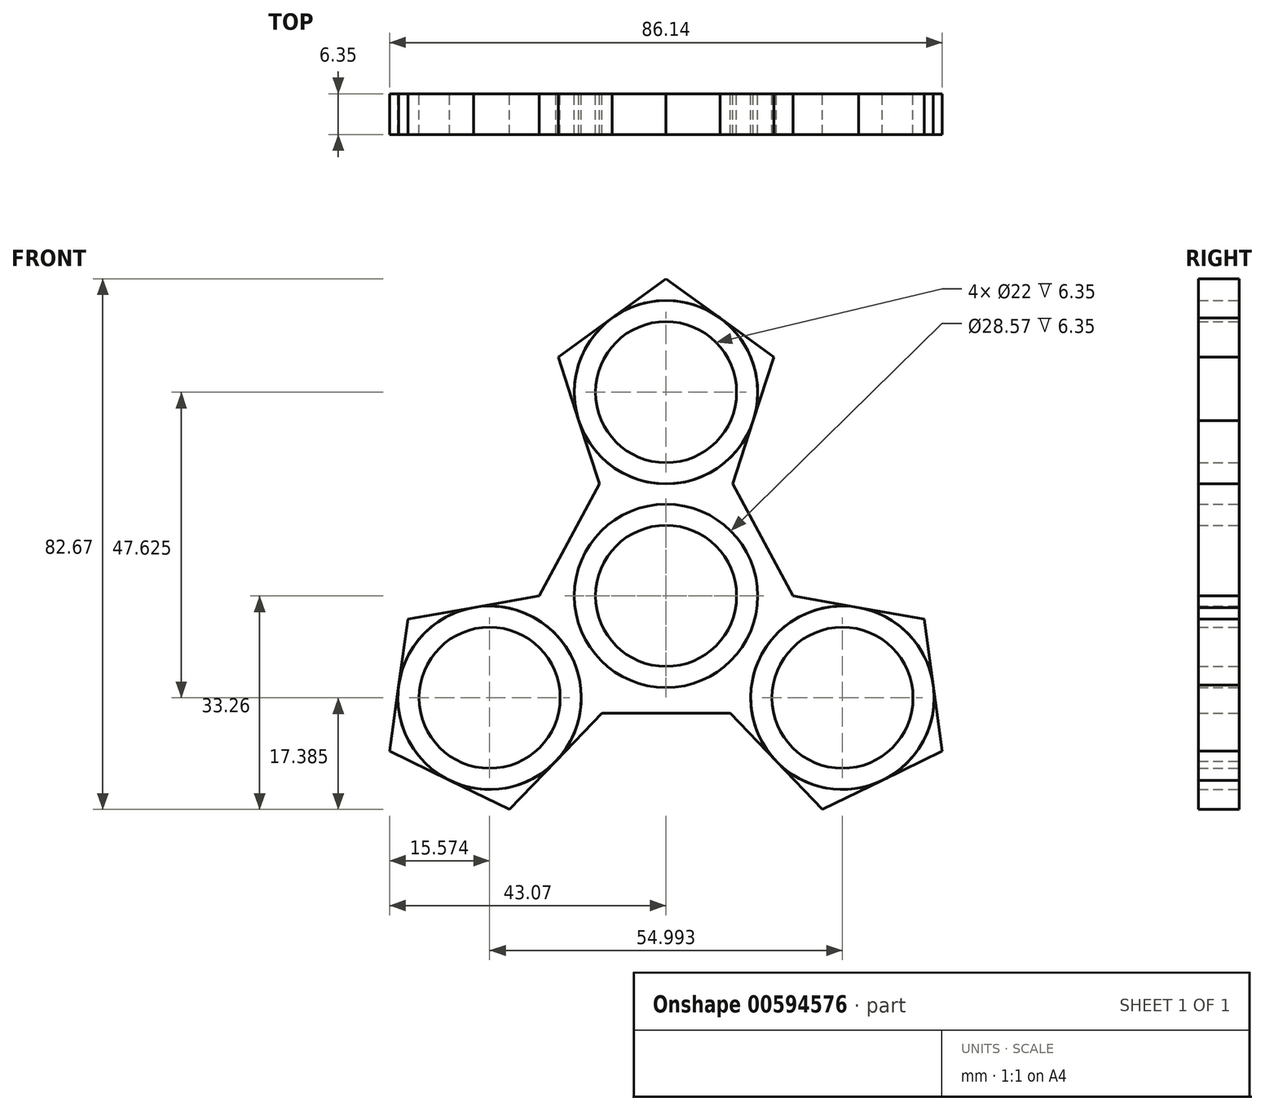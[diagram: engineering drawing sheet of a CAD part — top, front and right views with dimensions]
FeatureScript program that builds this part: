
annotation { "Feature Type Name" : "Feature", "Feature Type Description" : "" }
export const myFeature = defineFeature(function(context is Context, id is Id, definition is map)
    precondition{}
    {
        {
            var Q0;
            Q0=qCreatedBy(makeId("Front.planeOp"),FACE);
            var sketch = newSketch(context, id + "F0", { "sketchPlane" : qUnion([Q0])});
            skCircle(sketch, "E0", {"center": v(0, 31.75) * mm, "radius": 11 * mm});
            skCircle(sketch, "E1", {"center": v(0, 0) * mm, "radius": 11 * mm});
            skCircle(sketch, "E2", {"center": v(0, 31.75) * mm, "radius": 14.29 * mm});
            skCircle(sketch, "E3", {"center": v(0, 0) * mm, "radius": 14.29 * mm});
            skCircle(sketch, "E4.1.0", {"center": v(-27.5, -15.87) * mm, "radius": 14.29 * mm});
            skCircle(sketch, "E4.1.1", {"center": v(-27.5, -15.87) * mm, "radius": 11 * mm});
            skCircle(sketch, "E5.1.2.0", {"center": v(27.5, -15.88) * mm, "radius": 14.29 * mm});
            skCircle(sketch, "E5.2.2.0", {"center": v(27.5, -15.88) * mm, "radius": 11 * mm});
            skSolve(sketch);
        }
        {
            var Q0;
            Q0=qCreatedBy(makeId("Front.planeOp"),FACE);
            var sketch = newSketch(context, id + "F1", { "sketchPlane" : qUnion([Q0])});
            skCircle(sketch, "E6.0", {"center": v(0, 31.75) * mm, "radius": 14.29 * mm});
            skCircle(sketch, "E7.0", {"center": v(0, 31.75) * mm, "radius": 11 * mm});
            skCircle(sketch, "E8.0", {"center": v(0, 0) * mm, "radius": 14.29 * mm});
            skCircle(sketch, "E9.0", {"center": v(0, 0) * mm, "radius": 11 * mm});
            skCircle(sketch, "E10.0", {"center": v(-27.5, -15.87) * mm, "radius": 14.29 * mm});
            skCircle(sketch, "E11.0", {"center": v(-27.5, -15.87) * mm, "radius": 11 * mm});
            skCircle(sketch, "E12.0", {"center": v(27.5, -15.88) * mm, "radius": 14.29 * mm});
            skCircle(sketch, "E13.0", {"center": v(27.5, -15.88) * mm, "radius": 11 * mm});
            skCircle(sketch, "E14.cCircle", {"center": v(0, 31.75) * mm, "radius": 14.29 * mm, "construction": true});
            skLineSegment(sketch, "E14.0", {"start": v(10.38, 17.46) * mm, "end": v(-10.38, 17.46) * mm});
            skLineSegment(sketch, "E14.1", {"start": v(-10.38, 17.46) * mm, "end": v(-16.8, 37.2) * mm});
            skLineSegment(sketch, "E14.2", {"start": v(-16.8, 37.2) * mm, "end": v(0, 49.41) * mm});
            skLineSegment(sketch, "E14.3", {"start": v(0, 49.41) * mm, "end": v(16.8, 37.2) * mm});
            skLineSegment(sketch, "E14.4", {"start": v(16.8, 37.2) * mm, "end": v(10.38, 17.46) * mm});
            skPoint(sketch, "E14.0.midPoint", {"position": v(0, 17.46) * mm});
            skCircle(sketch, "E15.cCircle", {"center": v(-27.5, -15.87) * mm, "radius": 14.29 * mm, "construction": true});
            skLineSegment(sketch, "E15.0", {"start": v(-19.8, 0.02) * mm, "end": v(-10, -18.29) * mm});
            skLineSegment(sketch, "E15.1", {"start": v(-10, -18.29) * mm, "end": v(-24.38, -33.26) * mm});
            skLineSegment(sketch, "E15.2", {"start": v(-24.38, -33.26) * mm, "end": v(-43.07, -24.2) * mm});
            skLineSegment(sketch, "E15.3", {"start": v(-43.07, -24.2) * mm, "end": v(-40.23, -3.64) * mm});
            skLineSegment(sketch, "E15.4", {"start": v(-40.23, -3.64) * mm, "end": v(-19.8, 0.02) * mm});
            skPoint(sketch, "E15.0.midPoint", {"position": v(-14.9, -9.13) * mm});
            skCircle(sketch, "E16.cCircle", {"center": v(27.5, -15.88) * mm, "radius": 14.29 * mm, "construction": true});
            skLineSegment(sketch, "E16.0", {"start": v(10, -18.29) * mm, "end": v(19.8, 0.02) * mm});
            skLineSegment(sketch, "E16.1", {"start": v(19.8, 0.02) * mm, "end": v(40.23, -3.64) * mm});
            skLineSegment(sketch, "E16.2", {"start": v(40.23, -3.64) * mm, "end": v(43.07, -24.2) * mm});
            skLineSegment(sketch, "E16.3", {"start": v(43.07, -24.2) * mm, "end": v(24.38, -33.26) * mm});
            skLineSegment(sketch, "E16.4", {"start": v(24.38, -33.26) * mm, "end": v(10, -18.29) * mm});
            skPoint(sketch, "E16.0.midPoint", {"position": v(14.9, -9.13) * mm});
            skLineSegment(sketch, "E17", {"start": v(-10.38, 17.46) * mm, "end": v(-19.8, 0.02) * mm});
            skLineSegment(sketch, "E18", {"start": v(-10, -18.29) * mm, "end": v(10, -18.29) * mm});
            skLineSegment(sketch, "E19", {"start": v(19.8, 0.02) * mm, "end": v(10.38, 17.46) * mm});
            skSolve(sketch);
        }
        {
            var Q0;
            {var subQ0=sQuery(id+"F1.wireOp",EDGE,"E14.2");var subQ1=sQuery(id+"F1.wireOp",EDGE,"E6.0");var subQ2=makeQuery(id+"F1.imprint","INTERSECT",VERTEX,{"derivedFrom":[subQ1,subQ0]});Q0=makeQuery(id+"F1.imprint","IMPRINT",FACE,{"disambiguationData":[TD([[makeQuery(id+"F1.imprint","IMPRINT",EDGE,{"disambiguationData":[TD([[subQ2,1.0]])],"derivedFrom":subQ1}),-1.0]])]});}
            var Q1;
            {var subQ0=sQuery(id+"F1.wireOp",EDGE,"E14.3");var subQ1=sQuery(id+"F1.wireOp",EDGE,"E6.0");var subQ2=makeQuery(id+"F1.imprint","INTERSECT",VERTEX,{"derivedFrom":[subQ1,subQ0]});Q1=makeQuery(id+"F1.imprint","IMPRINT",FACE,{"disambiguationData":[TD([[makeQuery(id+"F1.imprint","IMPRINT",EDGE,{"disambiguationData":[TD([[subQ2,1.0]])],"derivedFrom":subQ1}),-1.0]])]});}
            var Q2;
            {var subQ0=sQuery(id+"F1.wireOp",EDGE,"E14.4");var subQ1=sQuery(id+"F1.wireOp",EDGE,"E6.0");var subQ2=makeQuery(id+"F1.imprint","INTERSECT",VERTEX,{"derivedFrom":[subQ1,subQ0]});Q2=makeQuery(id+"F1.imprint","IMPRINT",FACE,{"disambiguationData":[TD([[makeQuery(id+"F1.imprint","IMPRINT",EDGE,{"disambiguationData":[TD([[subQ2,1.0]])],"derivedFrom":subQ1}),-1.0]])]});}
            var Q3;
            {var subQ0=sQuery(id+"F1.wireOp",EDGE,"E14.1");var subQ1=sQuery(id+"F1.wireOp",EDGE,"E6.0");var subQ2=makeQuery(id+"F1.imprint","INTERSECT",VERTEX,{"derivedFrom":[subQ1,subQ0]});Q3=makeQuery(id+"F1.imprint","IMPRINT",FACE,{"disambiguationData":[TD([[makeQuery(id+"F1.imprint","IMPRINT",EDGE,{"disambiguationData":[TD([[subQ2,-1.0]])],"derivedFrom":subQ1}),-1.0]])]});}
            var Q4;
            {var subQ0=sQuery(id+"F1.wireOp",EDGE,"E14.2");var subQ1=sQuery(id+"F1.wireOp",EDGE,"E6.0");var subQ2=makeQuery(id+"F1.imprint","INTERSECT",VERTEX,{"derivedFrom":[subQ1,subQ0]});Q4=makeQuery(id+"F1.imprint","IMPRINT",FACE,{"disambiguationData":[TD([[makeQuery(id+"F1.imprint","IMPRINT",EDGE,{"disambiguationData":[TD([[subQ2,-1.0]])],"derivedFrom":subQ1}),-1.0]])]});}
            var Q5;
            Q5=makeQuery(id+"F0.imprint","IMPRINT",FACE,{"disambiguationData":[TD([[makeQuery(id+"F0.imprint","IMPRINT",EDGE,{"derivedFrom":sQuery(id+"F0.wireOp",EDGE,"E0")}),-1.0]])]});
            var Q6;
            Q6=makeQuery(id+"F1.imprint","IMPRINT",FACE,{"disambiguationData":[TD([[makeQuery(id+"F1.imprint","IMPRINT",EDGE,{"derivedFrom":sQuery(id+"F1.wireOp",EDGE,"E8.0")}),-1.0]])]});
            var Q7;
            Q7=makeQuery(id+"F0.imprint","IMPRINT",FACE,{"disambiguationData":[TD([[makeQuery(id+"F0.imprint","IMPRINT",EDGE,{"derivedFrom":sQuery(id+"F0.wireOp",EDGE,"E1")}),-1.0]])]});
            var Q8;
            {var subQ0=sQuery(id+"F1.wireOp",EDGE,"E16.2");var subQ1=sQuery(id+"F1.wireOp",EDGE,"E12.0");var subQ2=makeQuery(id+"F1.imprint","INTERSECT",VERTEX,{"derivedFrom":[subQ1,subQ0]});Q8=makeQuery(id+"F1.imprint","IMPRINT",FACE,{"disambiguationData":[TD([[makeQuery(id+"F1.imprint","IMPRINT",EDGE,{"disambiguationData":[TD([[subQ2,1.0]])],"derivedFrom":subQ1}),-1.0]])]});}
            var Q9;
            {var subQ0=sQuery(id+"F1.wireOp",EDGE,"E16.1");var subQ1=sQuery(id+"F1.wireOp",EDGE,"E12.0");var subQ2=makeQuery(id+"F1.imprint","INTERSECT",VERTEX,{"derivedFrom":[subQ1,subQ0]});Q9=makeQuery(id+"F1.imprint","IMPRINT",FACE,{"disambiguationData":[TD([[makeQuery(id+"F1.imprint","IMPRINT",EDGE,{"disambiguationData":[TD([[subQ2,-1.0]])],"derivedFrom":subQ1}),-1.0]])]});}
            var Q10;
            {var subQ0=sQuery(id+"F1.wireOp",EDGE,"E16.4");var subQ1=sQuery(id+"F1.wireOp",EDGE,"E12.0");var subQ2=makeQuery(id+"F1.imprint","INTERSECT",VERTEX,{"derivedFrom":[subQ1,subQ0]});Q10=makeQuery(id+"F1.imprint","IMPRINT",FACE,{"disambiguationData":[TD([[makeQuery(id+"F1.imprint","IMPRINT",EDGE,{"disambiguationData":[TD([[subQ2,1.0]])],"derivedFrom":subQ1}),-1.0]])]});}
            var Q11;
            {var subQ0=sQuery(id+"F1.wireOp",EDGE,"E16.3");var subQ1=sQuery(id+"F1.wireOp",EDGE,"E12.0");var subQ2=makeQuery(id+"F1.imprint","INTERSECT",VERTEX,{"derivedFrom":[subQ1,subQ0]});Q11=makeQuery(id+"F1.imprint","IMPRINT",FACE,{"disambiguationData":[TD([[makeQuery(id+"F1.imprint","IMPRINT",EDGE,{"disambiguationData":[TD([[subQ2,1.0]])],"derivedFrom":subQ1}),-1.0]])]});}
            var Q12;
            {var subQ0=sQuery(id+"F1.wireOp",EDGE,"E16.2");var subQ1=sQuery(id+"F1.wireOp",EDGE,"E12.0");var subQ2=makeQuery(id+"F1.imprint","INTERSECT",VERTEX,{"derivedFrom":[subQ1,subQ0]});Q12=makeQuery(id+"F1.imprint","IMPRINT",FACE,{"disambiguationData":[TD([[makeQuery(id+"F1.imprint","IMPRINT",EDGE,{"disambiguationData":[TD([[subQ2,-1.0]])],"derivedFrom":subQ1}),-1.0]])]});}
            var Q13;
            Q13=makeQuery(id+"F0.imprint","IMPRINT",FACE,{"disambiguationData":[TD([[makeQuery(id+"F0.imprint","IMPRINT",EDGE,{"derivedFrom":sQuery(id+"F0.wireOp",EDGE,"E5.1.2.0")}),1.0]])]});
            var Q14;
            {var subQ0=sQuery(id+"F1.wireOp",EDGE,"E15.2");var subQ1=sQuery(id+"F1.wireOp",EDGE,"E10.0");var subQ2=makeQuery(id+"F1.imprint","INTERSECT",VERTEX,{"derivedFrom":[subQ1,subQ0]});Q14=makeQuery(id+"F1.imprint","IMPRINT",FACE,{"disambiguationData":[TD([[makeQuery(id+"F1.imprint","IMPRINT",EDGE,{"disambiguationData":[TD([[subQ2,-1.0]])],"derivedFrom":subQ1}),-1.0]])]});}
            var Q15;
            {var subQ0=sQuery(id+"F1.wireOp",EDGE,"E15.2");var subQ1=sQuery(id+"F1.wireOp",EDGE,"E10.0");var subQ2=makeQuery(id+"F1.imprint","INTERSECT",VERTEX,{"derivedFrom":[subQ1,subQ0]});Q15=makeQuery(id+"F1.imprint","IMPRINT",FACE,{"disambiguationData":[TD([[makeQuery(id+"F1.imprint","IMPRINT",EDGE,{"disambiguationData":[TD([[subQ2,1.0]])],"derivedFrom":subQ1}),-1.0]])]});}
            var Q16;
            {var subQ0=sQuery(id+"F1.wireOp",EDGE,"E15.3");var subQ1=sQuery(id+"F1.wireOp",EDGE,"E10.0");var subQ2=makeQuery(id+"F1.imprint","INTERSECT",VERTEX,{"derivedFrom":[subQ1,subQ0]});Q16=makeQuery(id+"F1.imprint","IMPRINT",FACE,{"disambiguationData":[TD([[makeQuery(id+"F1.imprint","IMPRINT",EDGE,{"disambiguationData":[TD([[subQ2,1.0]])],"derivedFrom":subQ1}),-1.0]])]});}
            var Q17;
            {var subQ0=sQuery(id+"F1.wireOp",EDGE,"E15.4");var subQ1=sQuery(id+"F1.wireOp",EDGE,"E10.0");var subQ2=makeQuery(id+"F1.imprint","INTERSECT",VERTEX,{"derivedFrom":[subQ1,subQ0]});Q17=makeQuery(id+"F1.imprint","IMPRINT",FACE,{"disambiguationData":[TD([[makeQuery(id+"F1.imprint","IMPRINT",EDGE,{"disambiguationData":[TD([[subQ2,1.0]])],"derivedFrom":subQ1}),-1.0]])]});}
            var Q18;
            {var subQ0=sQuery(id+"F1.wireOp",EDGE,"E15.1");var subQ1=sQuery(id+"F1.wireOp",EDGE,"E10.0");var subQ2=makeQuery(id+"F1.imprint","INTERSECT",VERTEX,{"derivedFrom":[subQ1,subQ0]});Q18=makeQuery(id+"F1.imprint","IMPRINT",FACE,{"disambiguationData":[TD([[makeQuery(id+"F1.imprint","IMPRINT",EDGE,{"disambiguationData":[TD([[subQ2,-1.0]])],"derivedFrom":subQ1}),-1.0]])]});}
            var Q19;
            Q19=makeQuery(id+"F0.imprint","IMPRINT",FACE,{"disambiguationData":[TD([[makeQuery(id+"F0.imprint","IMPRINT",EDGE,{"derivedFrom":sQuery(id+"F0.wireOp",EDGE,"E4.1.0")}),1.0]])]});
            extrude(context, id + "F2", {"entities" : qUnion([Q0, Q1, Q2, Q3, Q4, Q5, Q6, Q7, Q8, Q9, Q10, Q11, Q12, Q13, Q14, Q15, Q16, Q17, Q18, Q19]), "depth" : 6.35 * mm, "offsetDistance" : 25.4 * mm});
        }
    });
